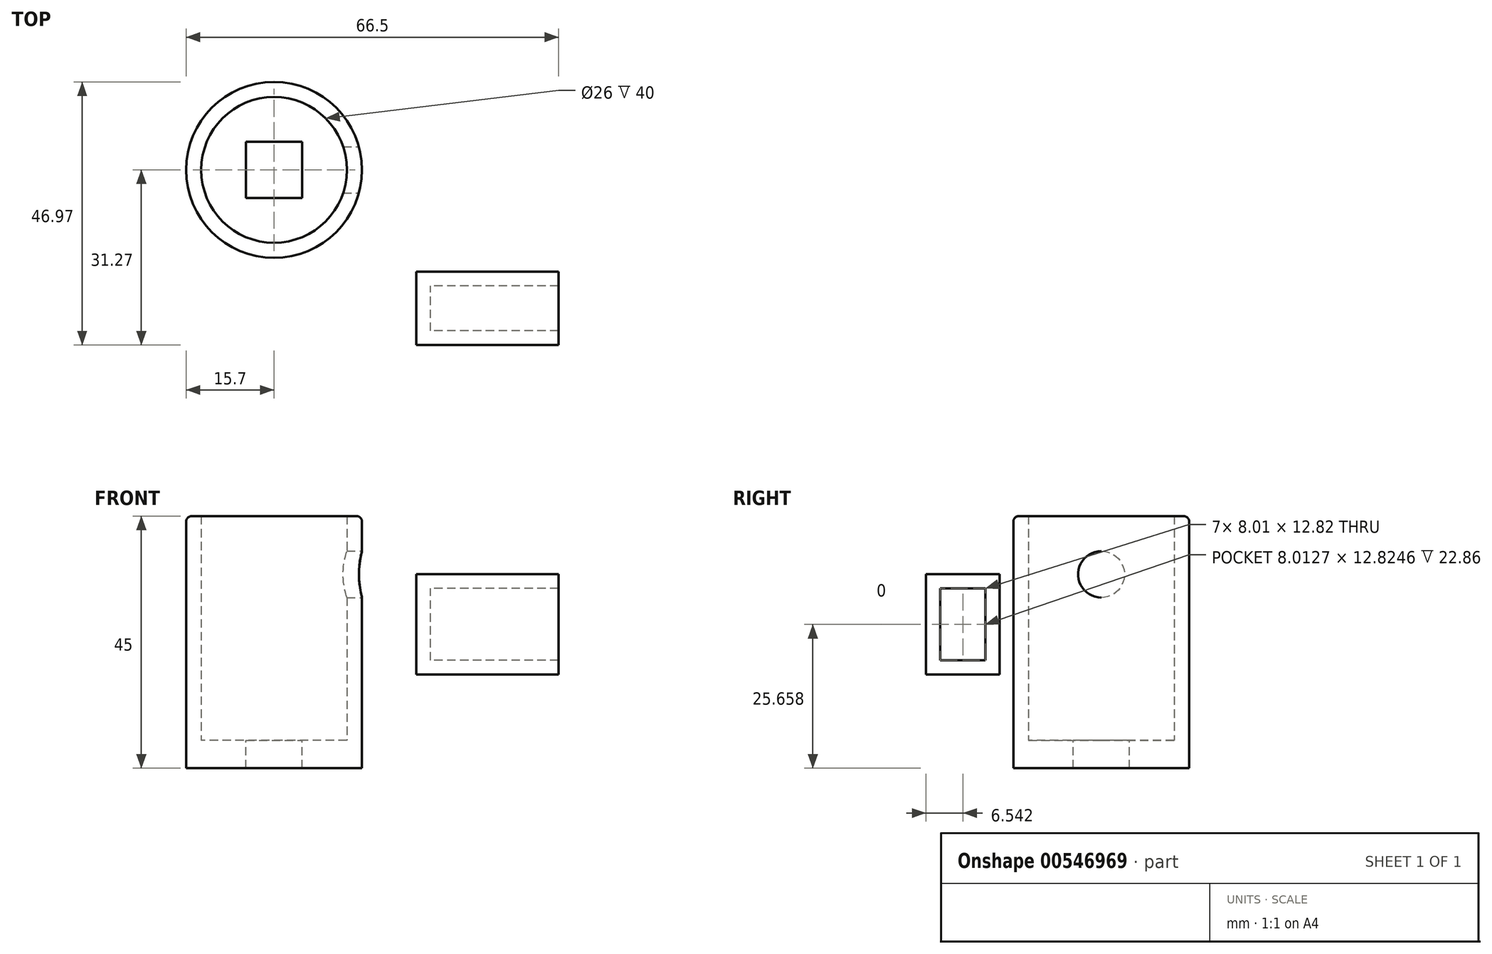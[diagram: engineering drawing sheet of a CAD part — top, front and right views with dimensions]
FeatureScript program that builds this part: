
annotation { "Feature Type Name" : "Feature", "Feature Type Description" : "" }
export const myFeature = defineFeature(function(context is Context, id is Id, definition is map)
    precondition{}
    {
        {
            var Q0;
            Q0=qCreatedBy(makeId("Top.planeOp"),FACE);
            var sketch = newSketch(context, id + "F0", { "sketchPlane" : qUnion([Q0])});
            skCircle(sketch, "E0", {"center": v(0, 0) * mm, "radius": 15.7 * mm});
            skSolve(sketch);
        }
        {
            var Q0;
            Q0=makeQuery(id+"F0.imprint","IMPRINT",FACE,{"disambiguationData":[TD([[makeQuery(id+"F0.imprint","IMPRINT",EDGE,{"derivedFrom":sQuery(id+"F0.wireOp",EDGE,"E0")}),1.0]])]});
            extrude(context, id + "F1", {"entities" : qUnion([Q0]), "depth" : 5 * mm, "offsetDistance" : 25.4 * mm});
        }
        {
            var Q0;
            Q0=makeQuery(id+"F1.opExtrude","CAP_FACE",FACE,{"disambiguationData":[OSD([sQuery(id+"F0.wireOp",EDGE,"E0")])],"isStart":false});
            var sketch = newSketch(context, id + "F2", { "sketchPlane" : qUnion([Q0])});
            skCircle(sketch, "E1", {"center": v(0, 0) * mm, "radius": 15.7 * mm});
            skCircle(sketch, "E2", {"center": v(0, 0) * mm, "radius": 13 * mm});
            skSolve(sketch);
        }
        {
            var Q0;
            Q0=makeQuery(id+"F2.imprint","IMPRINT",FACE,{"disambiguationData":[TD([[makeQuery(id+"F2.imprint","IMPRINT",EDGE,{"derivedFrom":sQuery(id+"F2.wireOp",EDGE,"E1")}),1.0]])]});
            extrude(context, id + "F3", {"entities" : qUnion([Q0]), "operationType" : NewBodyOperationType.ADD, "depth" : 40 * mm, "offsetDistance" : 25.4 * mm});
        }
        {
            var Q0;
            Q0=makeQuery(id+"F1.opExtrude","CAP_FACE",FACE,{"disambiguationData":[OSD([sQuery(id+"F0.wireOp",EDGE,"E0")])],"isStart":false});
            var sketch = newSketch(context, id + "F4", { "sketchPlane" : qUnion([Q0])});
            skLineSegment(sketch, "E3.bottom", {"start": v(-5, 5) * mm, "end": v(5, 5) * mm});
            skLineSegment(sketch, "E3.top", {"start": v(-5, -5) * mm, "end": v(5, -5) * mm});
            skLineSegment(sketch, "E3.left", {"start": v(-5, 5) * mm, "end": v(-5, -5) * mm});
            skLineSegment(sketch, "E3.right", {"start": v(5, 5) * mm, "end": v(5, -5) * mm});
            skPoint(sketch, "E4", {"position": v(0, 5) * mm});
            skPoint(sketch, "E5", {"position": v(-5, 0) * mm});
            skSolve(sketch);
        }
        {
            var Q0;
            Q0=makeQuery(id+"F4.imprint","IMPRINT",FACE,{"disambiguationData":[TD([[makeQuery(id+"F4.imprint","IMPRINT",EDGE,{"derivedFrom":sQuery(id+"F4.wireOp",EDGE,"E3.bottom")}),-1.0]])]});
            extrude(context, id + "F5", {"entities" : qUnion([Q0]), "operationType" : NewBodyOperationType.REMOVE, "oppositeDirection" : true, "depth" : 25.4 * mm, "offsetDistance" : 25.4 * mm});
        }
        {
            var Q0;
            Q0=makeQuery(id+"F3.opExtrude","CAP_EDGE",EDGE,{"disambiguationData":[OSD([sQuery(id+"F2.wireOp",EDGE,"E1")])],"isStart":false});
            fillet(context, id + "F6", {"entities" : qUnion([Q0]), "radius" : 1 * mm, "tangentPropagation" : true, "allowEdgeOverflow" : false});
        }
        {
            var Q0;
            Q0=qCreatedBy(makeId("Right.planeOp"),FACE);
            cPlane(context, id + "F7", {"entities" : qUnion([Q0]), "cplaneType" : CPlaneType.OFFSET, "offset" : 25.4 * mm, "width" : 152.4 * mm, "height" : 152.4 * mm});
        }
        {
            var Q0;
            Q0=qCreatedBy(id+"F7.planeOp",FACE);
            var sketch = newSketch(context, id + "F8", { "sketchPlane" : qUnion([Q0])});
            skCircle(sketch, "E6", {"center": v(0, 34.6) * mm, "radius": 4.15 * mm});
            skSolve(sketch);
        }
        {
            var Q0;
            Q0=makeQuery(id+"F8.imprint","IMPRINT",FACE,{"disambiguationData":[TD([[makeQuery(id+"F8.imprint","IMPRINT",EDGE,{"derivedFrom":sQuery(id+"F8.wireOp",EDGE,"E6")}),1.0]])]});
            extrude(context, id + "F9", {"entities" : qUnion([Q0]), "operationType" : NewBodyOperationType.REMOVE, "oppositeDirection" : true, "depth" : 25.4 * mm, "offsetDistance" : 25.4 * mm});
        }
        {
            var Q0;
            Q0=qCreatedBy(id+"F7.planeOp",FACE);
            var sketch = newSketch(context, id + "F10", { "sketchPlane" : qUnion([Q0])});
            skLineSegment(sketch, "E7.bottom", {"start": v(-31.27, 16.7) * mm, "end": v(-18.18, 16.7) * mm});
            skLineSegment(sketch, "E7.top", {"start": v(-31.27, 34.61) * mm, "end": v(-18.18, 34.61) * mm});
            skLineSegment(sketch, "E7.left", {"start": v(-31.27, 16.7) * mm, "end": v(-31.27, 34.61) * mm});
            skLineSegment(sketch, "E7.right", {"start": v(-18.18, 16.7) * mm, "end": v(-18.18, 34.61) * mm});
            skSolve(sketch);
        }
        {
            var Q0;
            Q0=makeQuery(id+"F10.imprint","IMPRINT",FACE,{"disambiguationData":[TD([[makeQuery(id+"F10.imprint","IMPRINT",EDGE,{"derivedFrom":sQuery(id+"F10.wireOp",EDGE,"E7.bottom")}),1.0]])]});
            extrude(context, id + "F11", {"entities" : qUnion([Q0]), "depth" : 25.4 * mm, "offsetDistance" : 25.4 * mm});
        }
        {
            var Q0;
            Q0=makeQuery(id+"F11.opExtrude","CAP_FACE",FACE,{"disambiguationData":[OSD([sQuery(id+"F10.wireOp",EDGE,"E7.bottom"),sQuery(id+"F10.wireOp",EDGE,"E7.top"),sQuery(id+"F10.wireOp",EDGE,"E7.left"),sQuery(id+"F10.wireOp",EDGE,"E7.right")])],"isStart":false});
            shell(context, id + "F12", {"entities" : qUnion([Q0]), "thickness" : 2.54 * mm});
        }
    });
